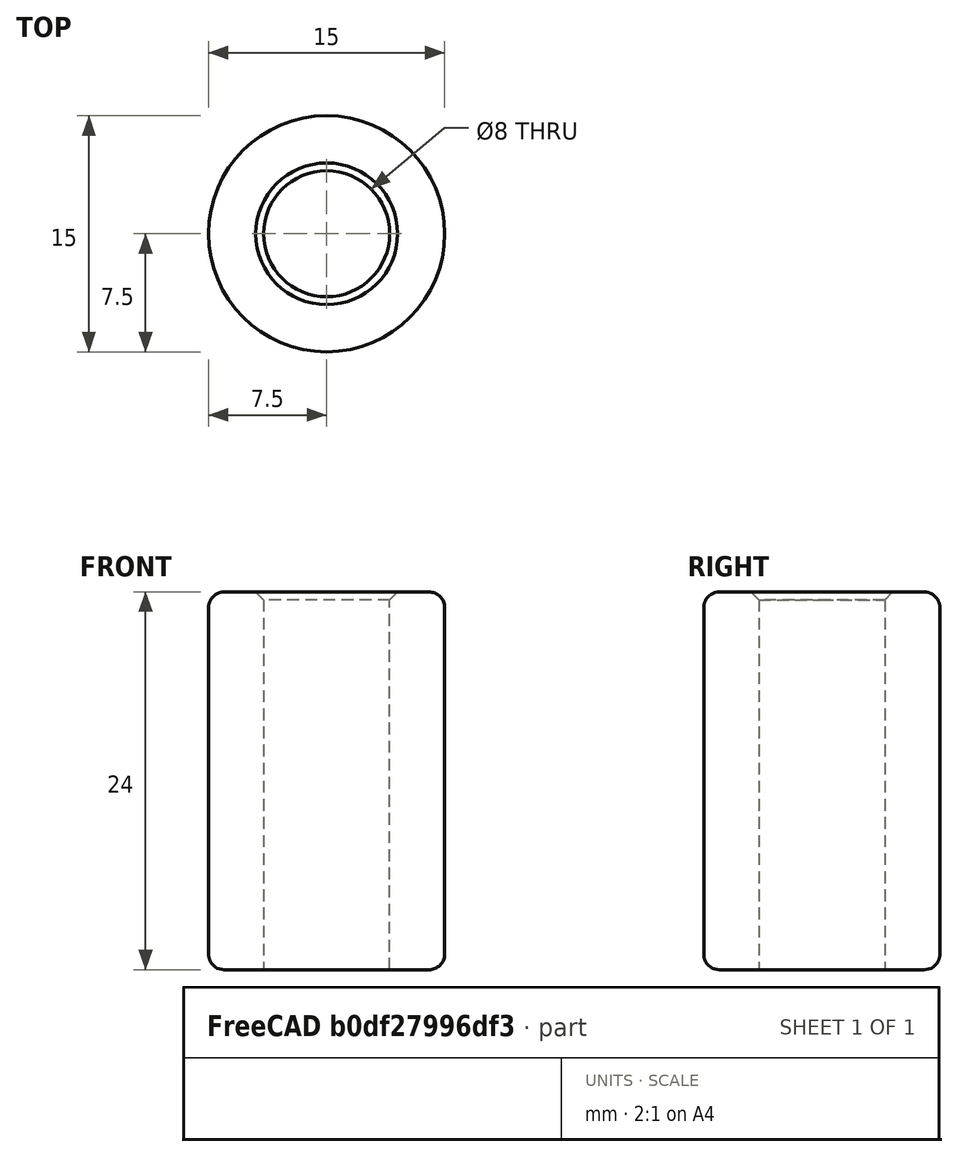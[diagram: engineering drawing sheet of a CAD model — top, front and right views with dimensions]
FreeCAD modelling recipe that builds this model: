
FCSTD DOCUMENT  (FreeCAD 0.14R3310 (Git))
Label: 77. COJINETE IGUS RJZM_02_08
License: CC-BY 3.0
LicenseURL: http://creativecommons.org/licenses/by/3.0/
objects: Sketcher::SketchObject×1, PartDesign::Pad×1, PartDesign::Fillet×1, PartDesign::Chamfer×1
note: 5 computed .brp shape members not serialized (recipe doc carries the construction recipe); baked Part::Feature solids carry a one-line shape summary decoded from their .brp

FEATURE [Sketcher::SketchObject] Sketch
  sketch-geometry (2):
    g0: Circle CenterX=0 CenterY=0 CenterZ=0 NormalX=0 NormalY=0 NormalZ=1 Radius=4
    g1: Circle CenterX=0 CenterY=0 CenterZ=0 NormalX=0 NormalY=0 NormalZ=1 Radius=7.5
  constraints (4):
    c: Coincident(g0,g-1)
    c: Coincident(g1,g-1)
    c: Radius(g1) = 7.5
    c: Radius(g0) = 4
FEATURE [PartDesign::Pad] Pad
  Length = 24
  Length2 = 100
  Sketch = -> Sketch
  Type = 0
FEATURE [PartDesign::Fillet] Fillet
  Base = -> Pad [Edge3,Edge2]
  Radius = 1
FEATURE [PartDesign::Chamfer] Chamfer
  Base = -> Fillet [Edge9]
  Size = 0.5
